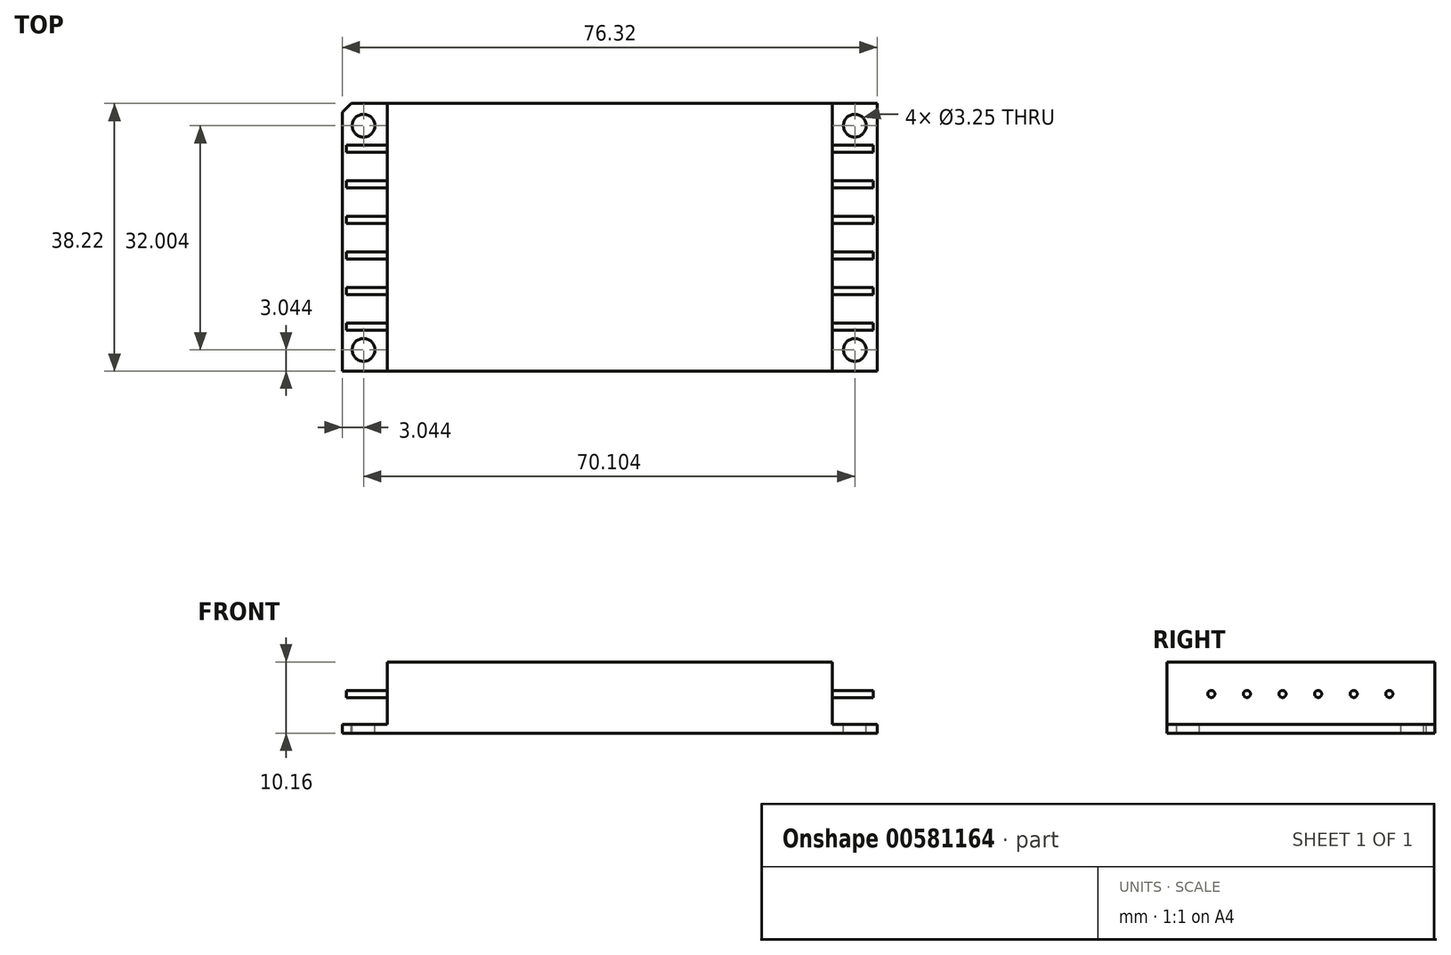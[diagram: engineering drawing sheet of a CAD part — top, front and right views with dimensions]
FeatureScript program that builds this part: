
annotation { "Feature Type Name" : "Feature", "Feature Type Description" : "" }
export const myFeature = defineFeature(function(context is Context, id is Id, definition is map)
    precondition{}
    {
        {
            var Q0;
            Q0=qCreatedBy(makeId("Top.planeOp"),FACE);
            var sketch = newSketch(context, id + "F0", { "sketchPlane" : qUnion([Q0])});
            skLineSegment(sketch, "E0.bottom", {"start": v(38.16, 19.11) * mm, "end": v(-38.16, 19.11) * mm});
            skLineSegment(sketch, "E0.top", {"start": v(38.16, -19.11) * mm, "end": v(-38.16, -19.11) * mm});
            skLineSegment(sketch, "E0.left", {"start": v(38.16, 19.11) * mm, "end": v(38.16, -19.11) * mm});
            skLineSegment(sketch, "E0.right", {"start": v(-38.16, 19.11) * mm, "end": v(-38.16, -19.11) * mm});
            skPoint(sketch, "E0.middle", {"position": v(0, 0) * mm});
            skSolve(sketch);
        }
        {
            var Q0;
            Q0 = qSketchRegion(id + "F0", true);
            extrude(context, id + "F1", {"entities" : qUnion([Q0]), "depth" : 1.27 * mm, "offsetDistance" : 25.4 * mm});
        }
        {
            var Q0;
            Q0=makeQuery(id+"F1.opExtrude","CAP_FACE",FACE,{"disambiguationData":[OSD([sQuery(id+"F0.wireOp",EDGE,"E0.bottom"),sQuery(id+"F0.wireOp",EDGE,"E0.top"),sQuery(id+"F0.wireOp",EDGE,"E0.left"),sQuery(id+"F0.wireOp",EDGE,"E0.right")])],"isStart":false});
            var sketch = newSketch(context, id + "F2", { "sketchPlane" : qUnion([Q0])});
            skLineSegment(sketch, "E1.bottom", {"start": v(31.75, 19.11) * mm, "end": v(-31.75, 19.11) * mm});
            skLineSegment(sketch, "E1.top", {"start": v(31.75, -19.11) * mm, "end": v(-31.75, -19.11) * mm});
            skLineSegment(sketch, "E1.left", {"start": v(31.75, 19.11) * mm, "end": v(31.75, -19.11) * mm});
            skLineSegment(sketch, "E1.right", {"start": v(-31.75, 19.11) * mm, "end": v(-31.75, -19.11) * mm});
            skPoint(sketch, "E1.middle", {"position": v(0, 0) * mm});
            skSolve(sketch);
        }
        {
            var Q0;
            Q0 = qSketchRegion(id + "F2", true);
            extrude(context, id + "F3", {"entities" : qUnion([Q0]), "operationType" : NewBodyOperationType.ADD, "depth" : 8.9 * mm, "offsetDistance" : 25.4 * mm});
        }
        {
            var Q0;
            {var subQ0=sQuery(id+"F0.wireOp",EDGE,"E0.left");var subQ1=sQuery(id+"F0.wireOp",EDGE,"E0.top");var subQ2=sQuery(id+"F0.wireOp",EDGE,"E0.bottom");Q0=makeQuery(id+"F3.boolean.opBoolean","SPLIT",FACE,{"disambiguationData":[TD([makeQuery(id+"F1.opExtrude","SWEPT_FACE",FACE,{"disambiguationData":[OSD([subQ0])]})])],"derivedFrom":makeQuery(id+"F1.opExtrude","CAP_FACE",FACE,{"disambiguationData":[OSD([subQ2,subQ1,subQ0,sQuery(id+"F0.wireOp",EDGE,"E0.right")])],"isStart":false})});}
            var sketch = newSketch(context, id + "F4", { "sketchPlane" : qUnion([Q0])});
            skPoint(sketch, "E2", {"position": v(34.99, -16.07) * mm});
            skPoint(sketch, "E3", {"position": v(34.99, 15.94) * mm});
            skSolve(sketch);
        }
        {
            var Q0;
            Q0=sQuery(id+"F4.wireOp",VERTEX,"E2");
            var Q1;
            Q1=makeQuery(id+"F1.opExtrude","SWEPT_BODY",BODY,{"disambiguationData":[OSD([sQuery(id+"F0.wireOp",EDGE,"E0.bottom"),sQuery(id+"F0.wireOp",EDGE,"E0.top"),sQuery(id+"F0.wireOp",EDGE,"E0.left"),sQuery(id+"F0.wireOp",EDGE,"E0.right")])]});
            hole(context, id + "F5", {"style" : HoleStyle.SIMPLE, "endStyle" : HoleEndStyle.THROUGH, "holeDiameter" : 3.25 * mm, "majorDiameter" : 6.35 * mm, "isTappedThrough" : true, "tappedDepth" : 12.7 * mm, "tapClearance" : 3, "locations" : qUnion([Q0]), "scope" : qUnion([Q1])});
        }
        {
            var Q0;
            Q0=sQuery(id+"F4.wireOp",VERTEX,"E3");
            var Q1;
            Q1=makeQuery(id+"F1.opExtrude","SWEPT_BODY",BODY,{"disambiguationData":[OSD([sQuery(id+"F0.wireOp",EDGE,"E0.bottom"),sQuery(id+"F0.wireOp",EDGE,"E0.top"),sQuery(id+"F0.wireOp",EDGE,"E0.left"),sQuery(id+"F0.wireOp",EDGE,"E0.right")])]});
            hole(context, id + "F6", {"style" : HoleStyle.SIMPLE, "endStyle" : HoleEndStyle.THROUGH, "holeDiameter" : 3.25 * mm, "majorDiameter" : 6.35 * mm, "isTappedThrough" : true, "tappedDepth" : 12.7 * mm, "tapClearance" : 3, "locations" : qUnion([Q0]), "scope" : qUnion([Q1])});
        }
        {
            var Q0;
            {var subQ0=sQuery(id+"F0.wireOp",EDGE,"E0.top");var subQ1=sQuery(id+"F0.wireOp",EDGE,"E0.right");var subQ2=sQuery(id+"F0.wireOp",EDGE,"E0.bottom");Q0=makeQuery(id+"F3.boolean.opBoolean","SPLIT",FACE,{"disambiguationData":[TD([makeQuery(id+"F1.opExtrude","SWEPT_FACE",FACE,{"disambiguationData":[OSD([subQ1])]})])],"derivedFrom":makeQuery(id+"F1.opExtrude","CAP_FACE",FACE,{"disambiguationData":[OSD([subQ2,subQ0,sQuery(id+"F0.wireOp",EDGE,"E0.left"),subQ1])],"isStart":false})});}
            var sketch = newSketch(context, id + "F7", { "sketchPlane" : qUnion([Q0])});
            skPoint(sketch, "E4", {"position": v(-35.12, 15.94) * mm});
            skPoint(sketch, "E5", {"position": v(-35.12, -16.07) * mm});
            skSolve(sketch);
        }
        {
            var Q0;
            Q0=sQuery(id+"F7.wireOp",VERTEX,"E5");
            var Q1;
            Q1=makeQuery(id+"F1.opExtrude","SWEPT_BODY",BODY,{"disambiguationData":[OSD([sQuery(id+"F0.wireOp",EDGE,"E0.bottom"),sQuery(id+"F0.wireOp",EDGE,"E0.top"),sQuery(id+"F0.wireOp",EDGE,"E0.left"),sQuery(id+"F0.wireOp",EDGE,"E0.right")])]});
            hole(context, id + "F8", {"style" : HoleStyle.SIMPLE, "endStyle" : HoleEndStyle.THROUGH, "holeDiameter" : 3.25 * mm, "majorDiameter" : 6.35 * mm, "isTappedThrough" : true, "tappedDepth" : 12.7 * mm, "tapClearance" : 3, "locations" : qUnion([Q0]), "scope" : qUnion([Q1])});
        }
        {
            var Q0;
            Q0=sQuery(id+"F7.wireOp",VERTEX,"E4");
            var Q1;
            Q1=makeQuery(id+"F1.opExtrude","SWEPT_BODY",BODY,{"disambiguationData":[OSD([sQuery(id+"F0.wireOp",EDGE,"E0.bottom"),sQuery(id+"F0.wireOp",EDGE,"E0.top"),sQuery(id+"F0.wireOp",EDGE,"E0.left"),sQuery(id+"F0.wireOp",EDGE,"E0.right")])]});
            hole(context, id + "F9", {"style" : HoleStyle.SIMPLE, "endStyle" : HoleEndStyle.THROUGH, "holeDiameter" : 3.25 * mm, "majorDiameter" : 6.35 * mm, "isTappedThrough" : true, "tappedDepth" : 12.7 * mm, "tapClearance" : 3, "locations" : qUnion([Q0]), "scope" : qUnion([Q1])});
        }
        {
            var Q0;
            Q0=makeQuery(id+"F3.opExtrude","SWEPT_FACE",FACE,{"disambiguationData":[OSD([sQuery(id+"F2.wireOp",EDGE,"E1.left")])]});
            var sketch = newSketch(context, id + "F10", { "sketchPlane" : qUnion([Q0])});
            skCircle(sketch, "E6", {"center": v(-12.76, 5.59) * mm, "radius": 0.5 * mm});
            skCircle(sketch, "E7", {"center": v(-7.68, 5.59) * mm, "radius": 0.5 * mm});
            skCircle(sketch, "E8", {"center": v(-2.6, 5.59) * mm, "radius": 0.5 * mm});
            skCircle(sketch, "E9", {"center": v(2.48, 5.59) * mm, "radius": 0.5 * mm});
            skCircle(sketch, "E10", {"center": v(7.56, 5.59) * mm, "radius": 0.5 * mm});
            skCircle(sketch, "E11", {"center": v(12.64, 5.59) * mm, "radius": 0.5 * mm});
            skSolve(sketch);
        }
        {
            var Q0;
            Q0=makeQuery(id+"F3.opExtrude","SWEPT_FACE",FACE,{"disambiguationData":[OSD([sQuery(id+"F2.wireOp",EDGE,"E1.right")])]});
            var sketch = newSketch(context, id + "F11", { "sketchPlane" : qUnion([Q0])});
            skCircle(sketch, "E12", {"center": v(-12.64, 5.59) * mm, "radius": 0.5 * mm});
            skCircle(sketch, "E13", {"center": v(-7.56, 5.59) * mm, "radius": 0.5 * mm});
            skCircle(sketch, "E14", {"center": v(-2.48, 5.59) * mm, "radius": 0.5 * mm});
            skCircle(sketch, "E15", {"center": v(2.6, 5.59) * mm, "radius": 0.5 * mm});
            skCircle(sketch, "E16", {"center": v(7.68, 5.59) * mm, "radius": 0.5 * mm});
            skCircle(sketch, "E17", {"center": v(12.76, 5.59) * mm, "radius": 0.5 * mm});
            skSolve(sketch);
        }
        {
            var Q0;
            Q0 = qSketchRegion(id + "F10", true);
            extrude(context, id + "F12", {"entities" : qUnion([Q0]), "operationType" : NewBodyOperationType.ADD, "depth" : 5.84 * mm, "offsetDistance" : 25.4 * mm});
        }
        {
            var Q0;
            Q0 = qSketchRegion(id + "F11", true);
            extrude(context, id + "F13", {"entities" : qUnion([Q0]), "operationType" : NewBodyOperationType.ADD, "depth" : 5.84 * mm, "offsetDistance" : 25.4 * mm});
        }
        {
            var Q0;
            Q0=makeQuery(id+"F1.opExtrude","SWEPT_EDGE",EDGE,{"disambiguationData":[OSD([sQuery(id+"F0.wireOp",EDGE,"E0.bottom"),sQuery(id+"F0.wireOp",EDGE,"E0.right")])]});
            chamfer(context, id + "F14", {"entities" : qUnion([Q0]), "width" : 1.27 * mm});
        }
    });
